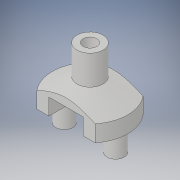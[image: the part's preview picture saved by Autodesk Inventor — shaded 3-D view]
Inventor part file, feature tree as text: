
AUTODESK INVENTOR PART (.ipt)
format: ipt  version: 2019.4 (Build 234330000, 330)  size: 164,864 bytes
history: native  units: mm
features: extrude x4, sketch x4, projected_geometry x2, chamfer x1
ambient origin geometry x8: Origin, YZ Plane, XZ Plane, XY Plane, X Axis, Y Axis, Z Axis, Center Point
bodies: Solid1 (feature_tree)
feature tree (11):
  extrude  "Extrusion1"  Depth=7.0mm
  extrude  "Extrusion2"  Depth=2.0mm
  extrude  "Extrusion3"  Depth=2.4mm
  chamfer  "Chamfer1"  Distance=7.5mm
  extrude  "Extrusion4"  Depth=6.4mm
  sketch  "Sketch1"  dims[d0=11.0mm d1=7.0mm]
  sketch  "Sketch2"  dims[d2=11.0mm d3=2.0mm]
  projected_geometry  "Projected Loop1"
  sketch  "Sketch3"  dims[d4=2.4mm d5=0.0mm d6=2.5mm]
  sketch  "Sketch5"  dims[d7=2.5mm d8=7.5mm d9=3.75mm d10=2.4mm d11=2.4mm d12=3.2mm d13=0.0mm d14=3.8mm d15=6.4mm d16=0.0mm d17=3.6mm d18=2.1mm d19=45.0deg d22=5.0mm d23=2.4mm d24=6.4mm d25=0.0mm]
  projected_geometry  "Projected Loop9"
